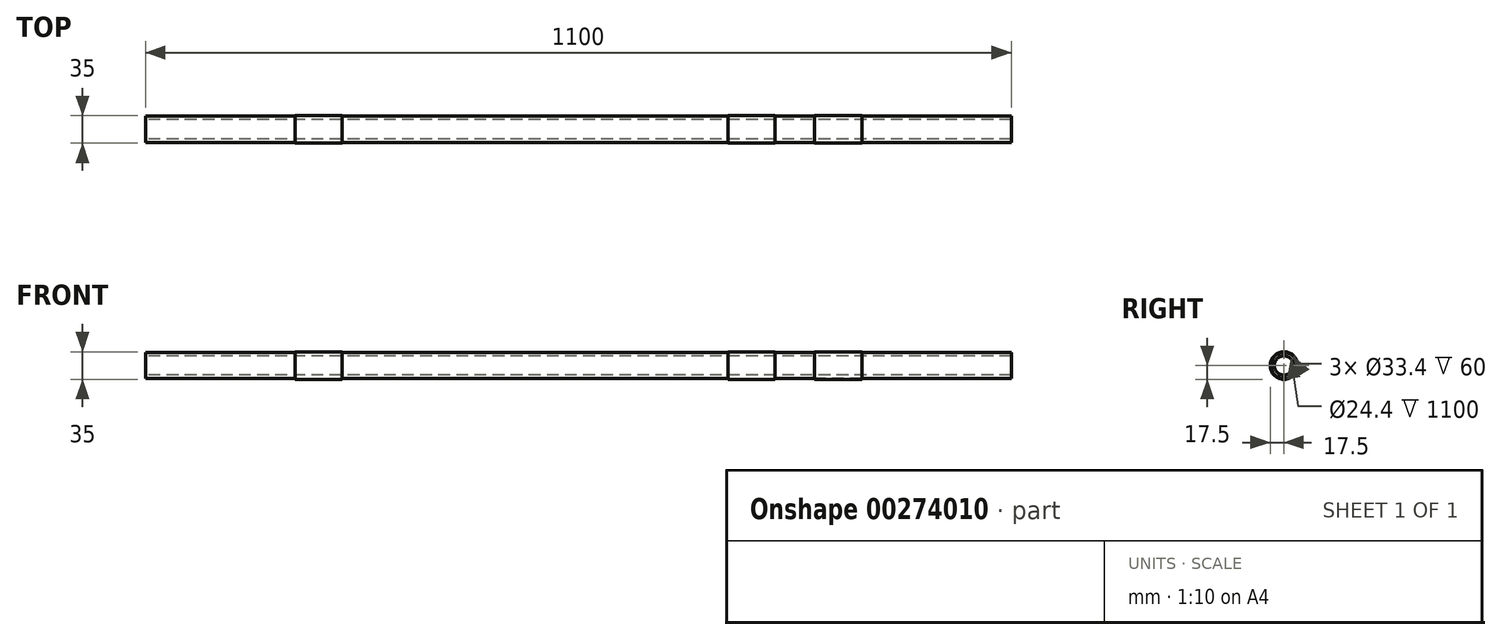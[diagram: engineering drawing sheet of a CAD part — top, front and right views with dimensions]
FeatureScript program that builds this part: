
annotation { "Feature Type Name" : "Feature", "Feature Type Description" : "" }
export const myFeature = defineFeature(function(context is Context, id is Id, definition is map)
    precondition{}
    {
        {
            var Q0;
            Q0=qCreatedBy(makeId("Right.planeOp"),FACE);
            var sketch = newSketch(context, id + "F0", { "sketchPlane" : qUnion([Q0])});
            skCircle(sketch, "E0", {"center": v(0, 0) * mm, "radius": 16.7 * mm});
            skCircle(sketch, "E1", {"center": v(0, 0) * mm, "radius": 12.2 * mm});
            skSolve(sketch);
        }
        {
            var Q0;
            Q0=qSketchRegion(id+"F0",true);
            extrude(context, id + "F1", {"entities" : qUnion([Q0]), "endBound" : BoundingType.SYMMETRIC, "depth" : 1100 * mm});
        }
        {
            var Q0;
            Q0=qCreatedBy(makeId("Right.planeOp"),FACE);
            var sketch = newSketch(context, id + "F2", { "sketchPlane" : qUnion([Q0])});
            skCircle(sketch, "E2.0", {"center": v(0, 0) * mm, "radius": 16.7 * mm});
            skCircle(sketch, "E3", {"center": v(0, 0) * mm, "radius": 17.5 * mm});
            skSolve(sketch);
        }
        {
            var Q0;
            Q0=qSketchRegion(id+"F2",true);
            extrude(context, id + "F3", {"entities" : qUnion([Q0]), "endBound" : BoundingType.SYMMETRIC, "depth" : 60 * mm});
        }
        {
            var Q0;
            Q0=makeQuery(id+"F3.opExtrude","SWEPT_BODY",BODY,{"disambiguationData":[OSD([sQuery(id+"F2.wireOp",EDGE,"E2.0"),sQuery(id+"F2.wireOp",EDGE,"E3")])]});
            transform(context, id + "F4", {"entities" : qUnion([Q0]), "transformType" : TransformType.TRANSLATION_3D, "dx" : 330 * mm, "dy" : 0 * mm, "dz" : 0 * mm, "makeCopy" : false});
        }
        {
            var Q0;
            Q0=makeQuery(id+"F3.opExtrude","SWEPT_BODY",BODY,{"disambiguationData":[OSD([sQuery(id+"F2.wireOp",EDGE,"E2.0"),sQuery(id+"F2.wireOp",EDGE,"E3")])]});
            var Q1;
            Q1=qCreatedBy(makeId("Right.planeOp"),FACE);
            mirror(context, id + "F5", {"entities" : qUnion([Q0]), "mirrorPlane" : qUnion([Q1])});
        }
        {
            var Q0;
            Q0=makeQuery(id+"F5.opPattern","COPY",BODY,{"derivedFrom":makeQuery(id+"F3.opExtrude","SWEPT_BODY",BODY,{"disambiguationData":[OSD([sQuery(id+"F2.wireOp",EDGE,"E2.0"),sQuery(id+"F2.wireOp",EDGE,"E3")])]}),"instanceName":"1"});
            transform(context, id + "F6", {"entities" : qUnion([Q0]), "transformType" : TransformType.TRANSLATION_3D, "dx" : 550 * mm, "dy" : 0 * mm, "dz" : 0 * mm, "makeCopy" : true});
        }
    });
